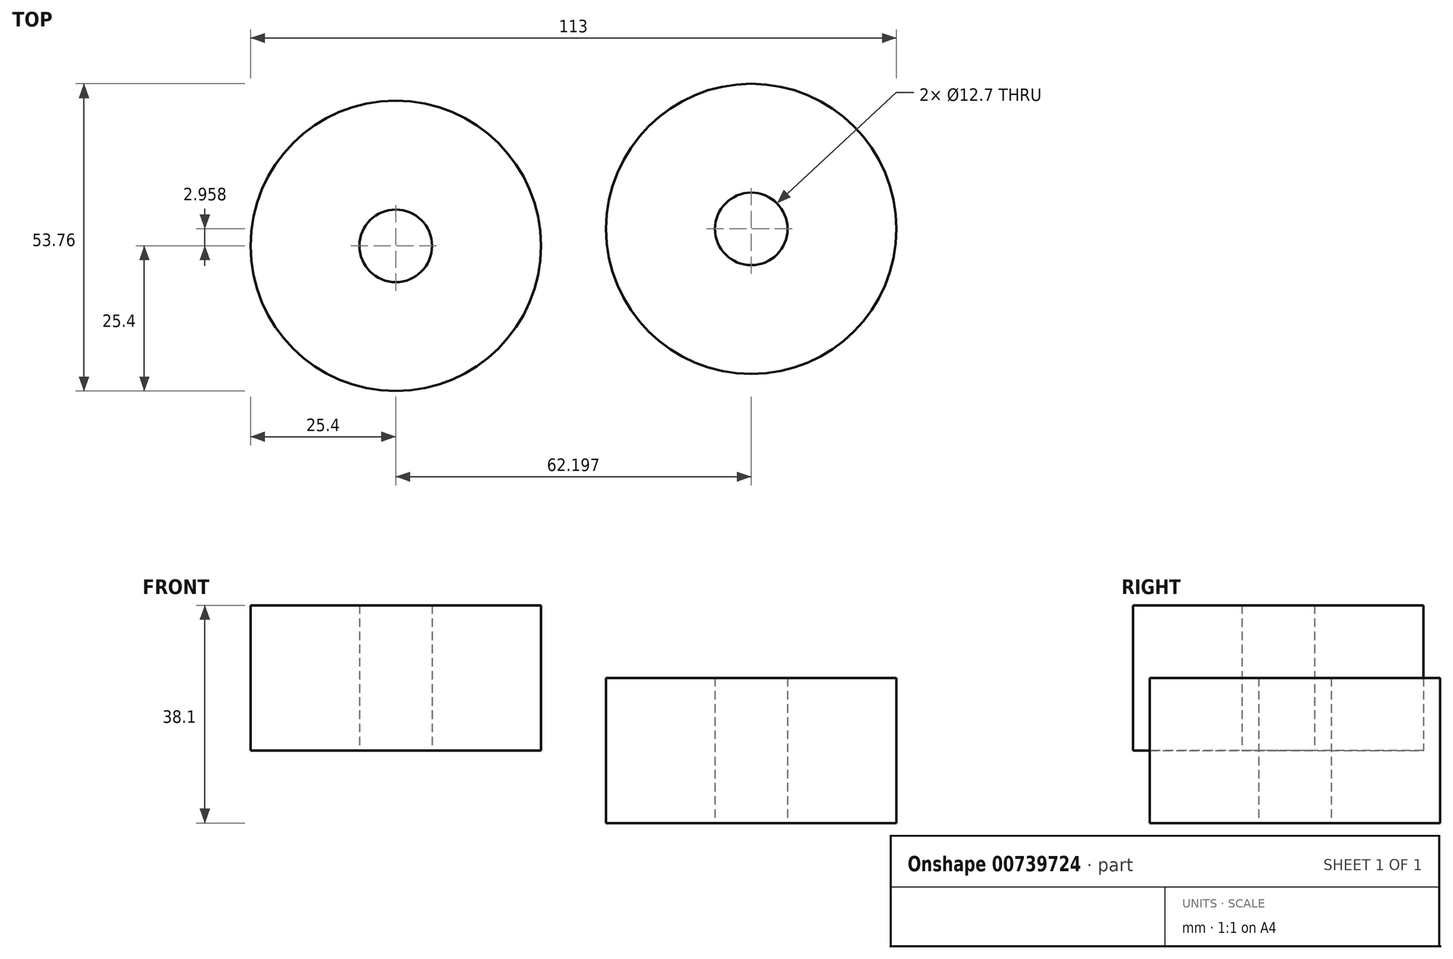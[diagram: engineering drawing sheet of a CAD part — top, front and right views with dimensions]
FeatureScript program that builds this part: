
annotation { "Feature Type Name" : "Feature", "Feature Type Description" : "" }
export const myFeature = defineFeature(function(context is Context, id is Id, definition is map)
    precondition{}
    {
        {
            var Q0;
            Q0=qCreatedBy(makeId("Top.planeOp"),FACE);
            var sketch = newSketch(context, id + "F0", { "sketchPlane" : qUnion([Q0])});
            skCircle(sketch, "E0", {"center": v(0, 0) * mm, "radius": 25.4 * mm});
            skCircle(sketch, "E1", {"center": v(0, 0) * mm, "radius": 6.35 * mm});
            skSolve(sketch);
        }
        {
            var Q0;
            Q0=makeQuery(id+"F0.imprint","IMPRINT",FACE,{"disambiguationData":[TD([[makeQuery(id+"F0.imprint","IMPRINT",EDGE,{"derivedFrom":sQuery(id+"F0.wireOp",EDGE,"E0")}),1.0]])]});
            extrude(context, id + "F1", {"entities" : qUnion([Q0]), "depth" : 25.4 * mm, "offsetDistance" : 25.4 * mm});
        }
        {
            var Q0;
            Q0=qCreatedBy(makeId("Top.planeOp"),FACE);
            var sketch = newSketch(context, id + "F2", { "sketchPlane" : qUnion([Q0])});
            skCircle(sketch, "E2", {"center": v(62.2, 2.96) * mm, "radius": 25.4 * mm});
            skCircle(sketch, "E3", {"center": v(62.2, 2.96) * mm, "radius": 6.35 * mm});
            skSolve(sketch);
        }
        {
            var Q0;
            Q0 = qSketchRegion(id + "F2", true);
            extrude(context, id + "F3", {"entities" : qUnion([Q0]), "endBound" : BoundingType.SYMMETRIC, "depth" : 25.4 * mm, "offsetDistance" : 25.4 * mm});
        }
    });
